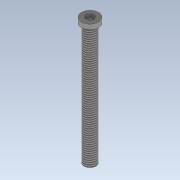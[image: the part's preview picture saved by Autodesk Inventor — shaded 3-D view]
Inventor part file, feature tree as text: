
AUTODESK INVENTOR PART (.ipt)
format: ipt  version: 2022 (Build 260153000, 153)  size: 121,344 bytes
history: native  units: mm
features: extrude x3, sketch x3, thread x1
ambient origin geometry x8: Origin, YZ Plane, XZ Plane, XY Plane, X Axis, Y Axis, Z Axis, Center Point
bodies: Solid1 (feature_tree)
feature tree (7):
  extrude  "Extrusion1"  Depth=50.0mm TaperAngle=0.0deg
  extrude  "Extrusion2"  Depth=2.0mm TaperAngle=0.0deg
  thread  "Thread1"  [1 undecoded]
  extrude  "Extrusion3"  Depth=1.0mm TaperAngle=0.0deg
  sketch  "Sketch1"  dims[d0=4.9mm d1=50.0mm d2=0.0mm]
  sketch  "Sketch2"  dims[d3=7.0mm d4=2.0mm d5=0.0mm d6=20.0mm d7=0.0mm]
  sketch  "Sketch3"  dims[d8=3.0mm d9=1.0mm d10=0.0mm]
note: 1 required parameter value undecoded (feature->parameter linkage not recoverable at this tier; creation-order binding heuristic only, values carry confidence <= 0.55)
